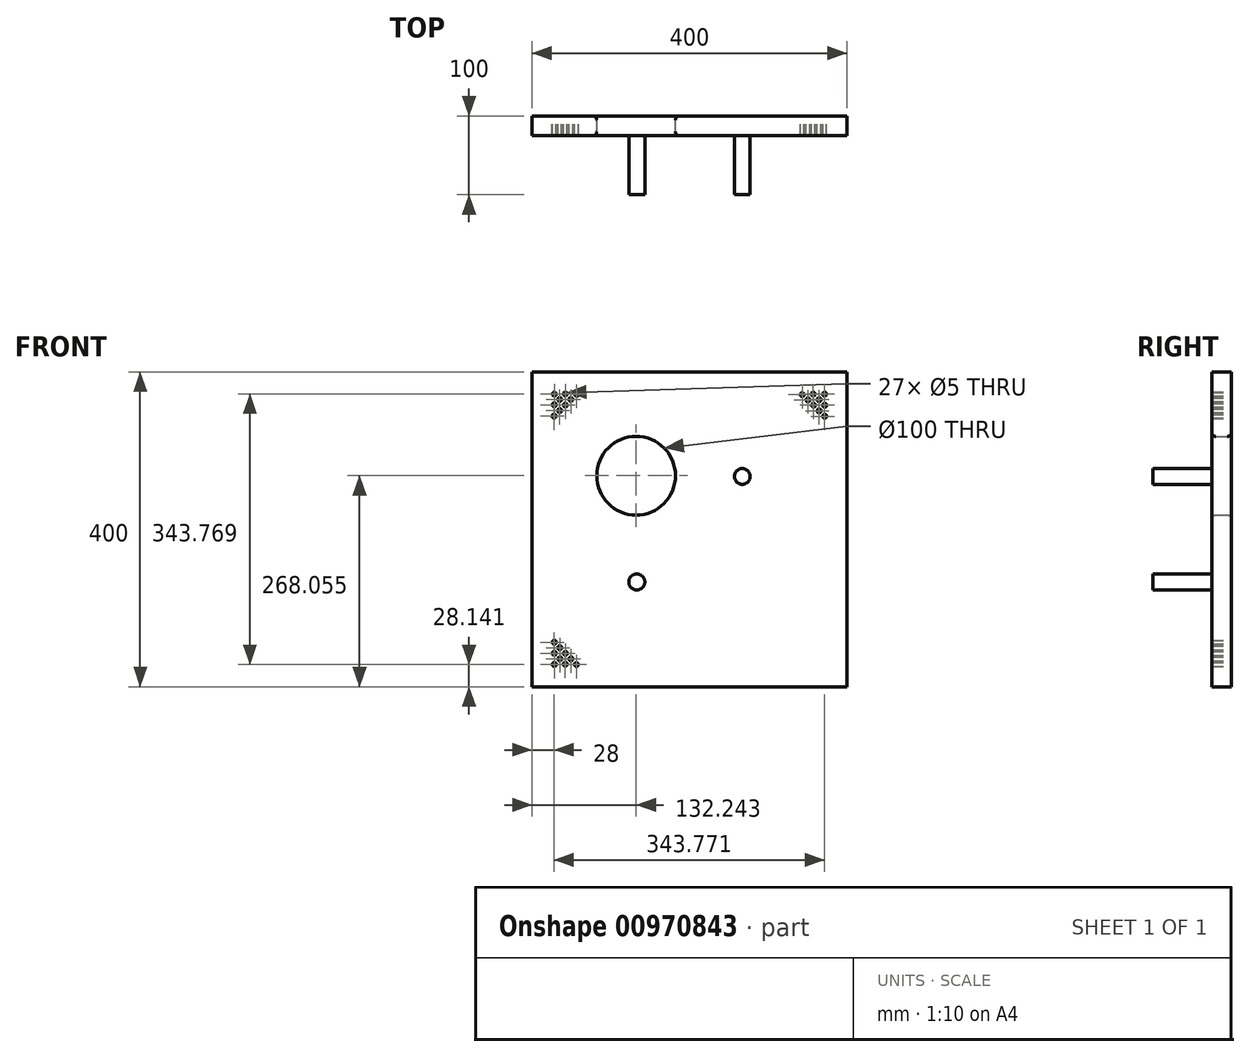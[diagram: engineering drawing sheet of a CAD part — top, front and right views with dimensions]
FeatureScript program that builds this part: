
annotation { "Feature Type Name" : "Feature", "Feature Type Description" : "" }
export const myFeature = defineFeature(function(context is Context, id is Id, definition is map)
    precondition{}
    {
        {
            var Q0;
            Q0=qCreatedBy(makeId("Front.planeOp"),FACE);
            var sketch = newSketch(context, id + "F0", { "sketchPlane" : qUnion([Q0])});
            skLineSegment(sketch, "E0.bottom", {"start": v(-211.24, -196.64) * mm, "end": v(188.76, -196.64) * mm});
            skLineSegment(sketch, "E0.top", {"start": v(-211.24, 203.36) * mm, "end": v(188.76, 203.36) * mm});
            skLineSegment(sketch, "E0.left", {"start": v(-211.24, -196.64) * mm, "end": v(-211.24, 203.36) * mm});
            skLineSegment(sketch, "E0.right", {"start": v(188.76, -196.64) * mm, "end": v(188.76, 203.36) * mm});
            skCircle(sketch, "E1", {"center": v(-79, 71.41) * mm, "radius": 50 * mm});
            skCircle(sketch, "E2", {"center": v(-78.12, -63.53) * mm, "radius": 10.23 * mm});
            skCircle(sketch, "E3", {"center": v(55.84, 70.43) * mm, "radius": 10 * mm});
            skCircle(sketch, "E4", {"center": v(-182.95, -168.36) * mm, "radius": 2.5 * mm});
            skCircle(sketch, "E5", {"center": v(-175.88, -161.29) * mm, "radius": 2.5 * mm});
            skCircle(sketch, "E6", {"center": v(-168.8, -154.22) * mm, "radius": 2.5 * mm});
            skCircle(sketch, "E7", {"center": v(-182.95, -154.22) * mm, "radius": 2.5 * mm});
            skCircle(sketch, "E8", {"center": v(-169.09, -168.16) * mm, "radius": 2.5 * mm});
            skCircle(sketch, "E9", {"center": v(-175.88, -147.14) * mm, "radius": 2.5 * mm});
            skCircle(sketch, "E10", {"center": v(-154.8, -168.5) * mm, "radius": 2.5 * mm});
            skCircle(sketch, "E11", {"center": v(-182.98, -140.1) * mm, "radius": 2.5 * mm});
            skCircle(sketch, "E12", {"center": v(-161.78, -161.33) * mm, "radius": 2.5 * mm});
            skCircle(sketch, "E13", {"center": v(160.48, 175.07) * mm, "radius": 2.5 * mm});
            skCircle(sketch, "E14", {"center": v(153.43, 167.99) * mm, "radius": 2.5 * mm});
            skCircle(sketch, "E15", {"center": v(146.36, 160.91) * mm, "radius": 2.5 * mm});
            skCircle(sketch, "E16", {"center": v(160.5, 160.91) * mm, "radius": 2.5 * mm});
            skCircle(sketch, "E17", {"center": v(145.94, 175.1) * mm, "radius": 2.5 * mm});
            skCircle(sketch, "E18", {"center": v(153.43, 153.84) * mm, "radius": 2.5 * mm});
            skCircle(sketch, "E19", {"center": v(131.99, 174.48) * mm, "radius": 2.5 * mm});
            skCircle(sketch, "E20", {"center": v(160.53, 146.8) * mm, "radius": 2.5 * mm});
            skCircle(sketch, "E21", {"center": v(139.28, 167.64) * mm, "radius": 2.5 * mm});
            skCircle(sketch, "E22", {"center": v(-182.93, 175.1) * mm, "radius": 2.5 * mm});
            skCircle(sketch, "E23", {"center": v(-176.03, 168.2) * mm, "radius": 2.5 * mm});
            skCircle(sketch, "E24", {"center": v(-168.96, 161.13) * mm, "radius": 2.5 * mm});
            skCircle(sketch, "E25", {"center": v(-168.96, 175.27) * mm, "radius": 2.5 * mm});
            skCircle(sketch, "E26", {"center": v(-182.9, 161.4) * mm, "radius": 2.5 * mm});
            skCircle(sketch, "E27", {"center": v(-161.89, 168.2) * mm, "radius": 2.5 * mm});
            skCircle(sketch, "E28", {"center": v(-183.24, 147.13) * mm, "radius": 2.5 * mm});
            skCircle(sketch, "E29", {"center": v(-154.48, 174.92) * mm, "radius": 2.5 * mm});
            skCircle(sketch, "E30", {"center": v(-176.07, 154.1) * mm, "radius": 2.5 * mm});
            skSolve(sketch);
        }
        {
            var Q0;
            Q0=makeQuery(id+"F0.imprint","IMPRINT",FACE,{"disambiguationData":[TD([[makeQuery(id+"F0.imprint","IMPRINT",EDGE,{"derivedFrom":sQuery(id+"F0.wireOp",EDGE,"E0.bottom")}),1.0]])]});
            extrude(context, id + "F1", {"entities" : qUnion([Q0]), "depth" : 25 * mm, "offsetDistance" : 25 * mm});
        }
        {
            var Q0;
            Q0=makeQuery(id+"F1.opExtrude","CAP_EDGE",EDGE,{"disambiguationData":[OSD([sQuery(id+"F0.wireOp",EDGE,"E1")])],"isStart":true});
            var Q1;
            Q1=makeQuery(id+"F1.opExtrude","CAP_EDGE",EDGE,{"disambiguationData":[OSD([sQuery(id+"F0.wireOp",EDGE,"E1")])],"isStart":false});
            fillet(context, id + "F2", {"entities" : qUnion([Q0, Q1]), "radius" : 5 * mm, "tangentPropagation" : true, "allowEdgeOverflow" : false});
        }
        {
            var Q0;
            Q0=makeQuery(id+"F0.imprint","IMPRINT",FACE,{"disambiguationData":[TD([[makeQuery(id+"F0.imprint","IMPRINT",EDGE,{"derivedFrom":sQuery(id+"F0.wireOp",EDGE,"E3")}),1.0]])]});
            var Q1;
            Q1=makeQuery(id+"F0.imprint","IMPRINT",FACE,{"disambiguationData":[TD([[makeQuery(id+"F0.imprint","IMPRINT",EDGE,{"derivedFrom":sQuery(id+"F0.wireOp",EDGE,"E2")}),1.0]])]});
            extrude(context, id + "F3", {"entities" : qUnion([Q0, Q1]), "operationType" : NewBodyOperationType.ADD, "depth" : 100 * mm, "offsetDistance" : 25 * mm});
        }
    });
